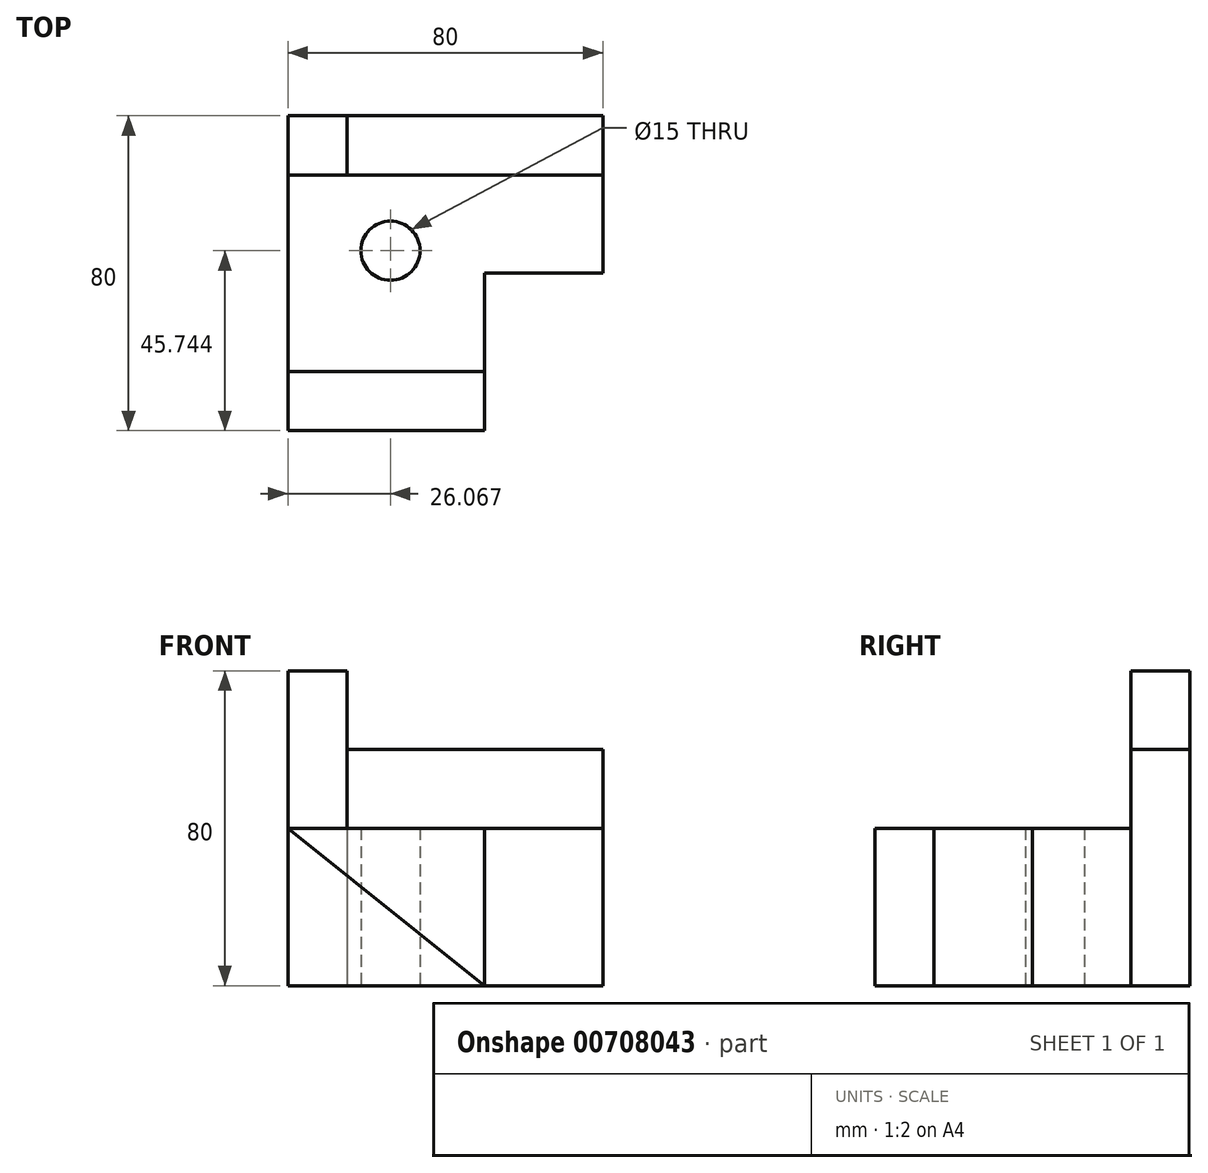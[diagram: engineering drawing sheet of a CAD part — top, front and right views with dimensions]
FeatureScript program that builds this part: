
annotation { "Feature Type Name" : "Feature", "Feature Type Description" : "" }
export const myFeature = defineFeature(function(context is Context, id is Id, definition is map)
    precondition{}
    {
        {
            var Q0;
            Q0=qCreatedBy(makeId("Front.planeOp"),FACE);
            var sketch = newSketch(context, id + "F0", { "sketchPlane" : qUnion([Q0])});
            skLineSegment(sketch, "E0", {"start": v(0, 0) * mm, "end": v(0, 40) * mm});
            skLineSegment(sketch, "E1", {"start": v(0, 0) * mm, "end": v(50, 0) * mm});
            skLineSegment(sketch, "E2", {"start": v(50, 0) * mm, "end": v(0, 40) * mm});
            skSolve(sketch);
        }
        {
            var Q0;
            Q0 = qSketchRegion(id + "F0", true);
            extrude(context, id + "F1", {"entities" : qUnion([Q0]), "depth" : 15 * mm, "offsetDistance" : 25 * mm});
        }
        {
            var Q0;
            Q0=qCreatedBy(makeId("Top.planeOp"),FACE);
            var sketch = newSketch(context, id + "F2", { "sketchPlane" : qUnion([Q0])});
            skLineSegment(sketch, "E3", {"start": v(0, 0) * mm, "end": v(0, 50) * mm});
            skLineSegment(sketch, "E4", {"start": v(0, 50) * mm, "end": v(80, 50) * mm});
            skLineSegment(sketch, "E5", {"start": v(80, 50) * mm, "end": v(80, 25) * mm});
            skLineSegment(sketch, "E6", {"start": v(80, 25) * mm, "end": v(50, 25) * mm});
            skLineSegment(sketch, "E7", {"start": v(50, 25) * mm, "end": v(50, 0) * mm});
            skLineSegment(sketch, "E8", {"start": v(0, 0) * mm, "end": v(50, 0) * mm});
            skSolve(sketch);
        }
        {
            var Q0;
            Q0 = qSketchRegion(id + "F2", true);
            extrude(context, id + "F3", {"entities" : qUnion([Q0]), "depth" : 40 * mm, "offsetDistance" : 25 * mm});
        }
        {
            var Q0;
            Q0=qCreatedBy(makeId("Top.planeOp"),FACE);
            var sketch = newSketch(context, id + "F4", { "sketchPlane" : qUnion([Q0])});
            skLineSegment(sketch, "E9", {"start": v(0, 0) * mm, "end": v(0, 50) * mm});
            skLineSegment(sketch, "E10", {"start": v(0, 50) * mm, "end": v(0, 65) * mm});
            skLineSegment(sketch, "E11", {"start": v(0, 65) * mm, "end": v(15, 65) * mm});
            skLineSegment(sketch, "E12", {"start": v(15, 65) * mm, "end": v(15, 50) * mm});
            skLineSegment(sketch, "E13", {"start": v(15, 50) * mm, "end": v(0, 50) * mm});
            skSolve(sketch);
        }
        {
            var Q0;
            Q0=makeQuery(id+"F4.imprint","IMPRINT",FACE,{"disambiguationData":[TD([[makeQuery(id+"F4.imprint","IMPRINT",EDGE,{"derivedFrom":sQuery(id+"F4.wireOp",EDGE,"E10")}),-1.0]])]});
            extrude(context, id + "F5", {"entities" : qUnion([Q0]), "depth" : 80 * mm, "offsetDistance" : 25 * mm});
        }
        {
            var Q0;
            Q0=qCreatedBy(makeId("Top.planeOp"),FACE);
            var sketch = newSketch(context, id + "F6", { "sketchPlane" : qUnion([Q0])});
            skLineSegment(sketch, "E14", {"start": v(15, 65) * mm, "end": v(80, 65) * mm});
            skLineSegment(sketch, "E15", {"start": v(80, 65) * mm, "end": v(80, 50) * mm});
            skLineSegment(sketch, "E16", {"start": v(80, 50) * mm, "end": v(15, 50) * mm});
            skLineSegment(sketch, "E17", {"start": v(15, 50) * mm, "end": v(15, 65) * mm});
            skSolve(sketch);
        }
        {
            var Q0;
            Q0=makeQuery(id+"F6.imprint","IMPRINT",FACE,{"disambiguationData":[TD([[makeQuery(id+"F6.imprint","IMPRINT",EDGE,{"derivedFrom":sQuery(id+"F6.wireOp",EDGE,"E14")}),-1.0]])]});
            extrude(context, id + "F7", {"entities" : qUnion([Q0]), "depth" : 60 * mm, "offsetDistance" : 25 * mm});
        }
        {
            var Q0;
            Q0=qCreatedBy(makeId("Top.planeOp"),FACE);
            var sketch = newSketch(context, id + "F8", { "sketchPlane" : qUnion([Q0])});
            skCircle(sketch, "E18", {"center": v(26.07, 30.74) * mm, "radius": 7.5 * mm});
            skSolve(sketch);
        }
        {
            var Q0;
            Q0 = qSketchRegion(id + "F8", true);
            extrude(context, id + "F9", {"entities" : qUnion([Q0]), "operationType" : NewBodyOperationType.REMOVE, "endBound" : BoundingType.UP_TO_NEXT, "depth" : 25 * mm, "offsetDistance" : 25 * mm});
        }
    });
